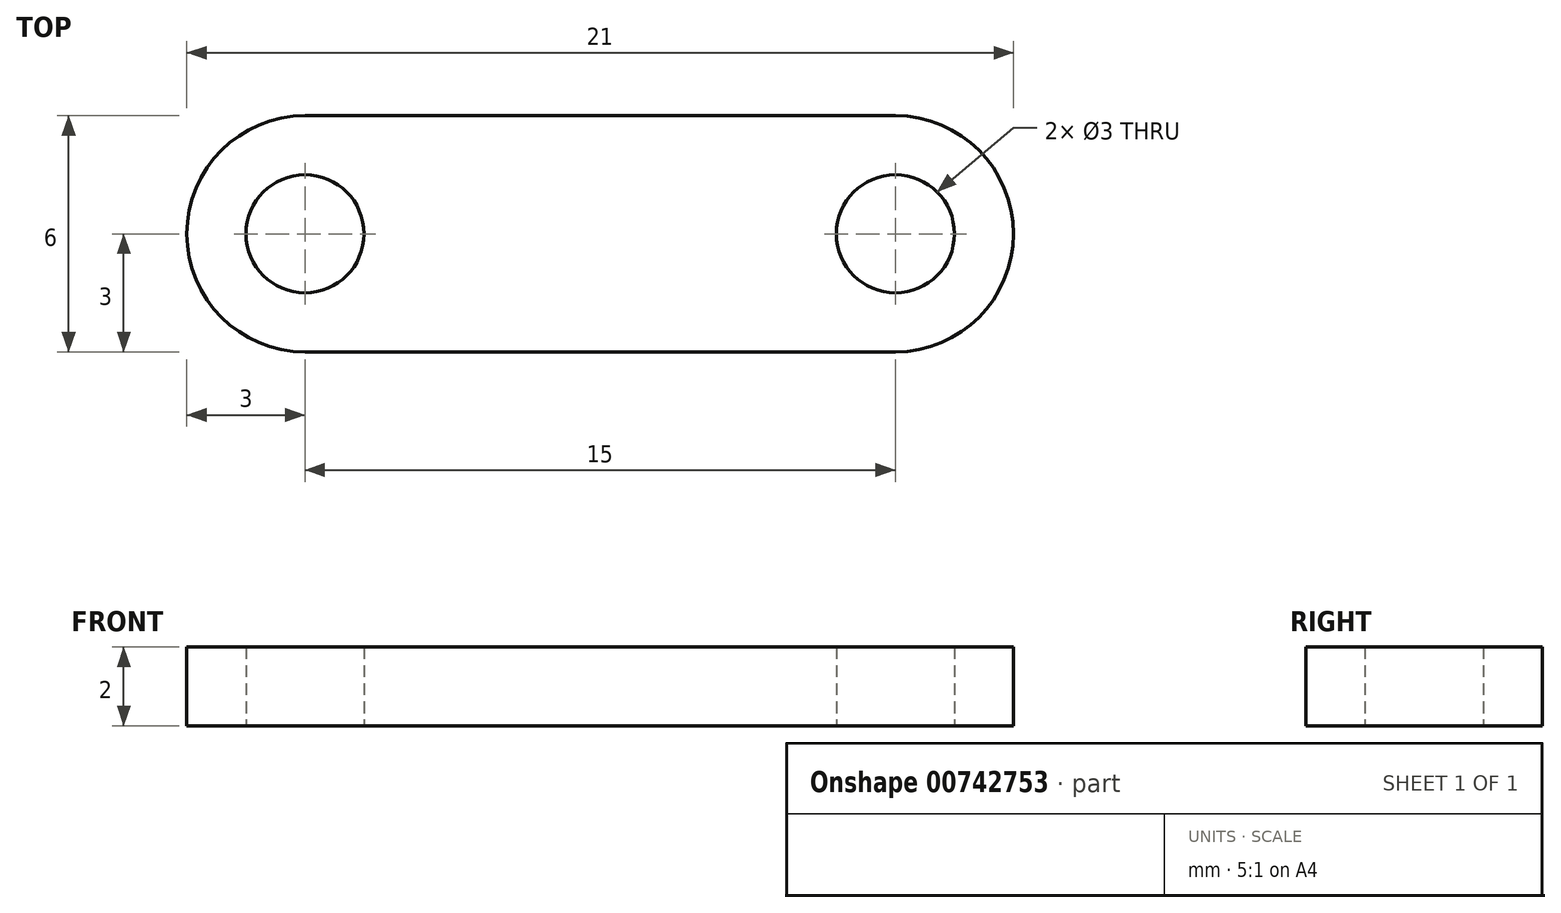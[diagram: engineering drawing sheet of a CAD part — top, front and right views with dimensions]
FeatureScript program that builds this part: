
annotation { "Feature Type Name" : "Feature", "Feature Type Description" : "" }
export const myFeature = defineFeature(function(context is Context, id is Id, definition is map)
    precondition{}
    {
        {
            var Q0;
            Q0=qCreatedBy(makeId("Top.planeOp"),FACE);
            var sketch = newSketch(context, id + "F0", { "sketchPlane" : qUnion([Q0])});
            skLineSegment(sketch, "E0.bottom", {"start": v(7.5, -3) * mm, "end": v(-7.5, -3) * mm});
            skLineSegment(sketch, "E0.top", {"start": v(7.5, 3) * mm, "end": v(-7.5, 3) * mm});
            skPoint(sketch, "E0.middle", {"position": v(0, 0) * mm});
            skArc(sketch, "E1", {"start": v(-7.5, 3) * mm, "mid": v(-10.5, 0) * mm, "end": v(-7.5, -3) * mm});
            skArc(sketch, "E2", {"start": v(7.5, -3) * mm, "mid": v(10.5, 0) * mm, "end": v(7.5, 3) * mm});
            skCircle(sketch, "E3", {"center": v(-7.5, 0) * mm, "radius": 1.5 * mm});
            skCircle(sketch, "E4", {"center": v(7.5, 0) * mm, "radius": 1.5 * mm});
            skSolve(sketch);
        }
        {
            var Q0;
            Q0 = qSketchRegion(id + "F0", true);
            extrude(context, id + "F1", {"entities" : qUnion([Q0]), "depth" : 2 * mm, "offsetDistance" : 25 * mm});
        }
    });
